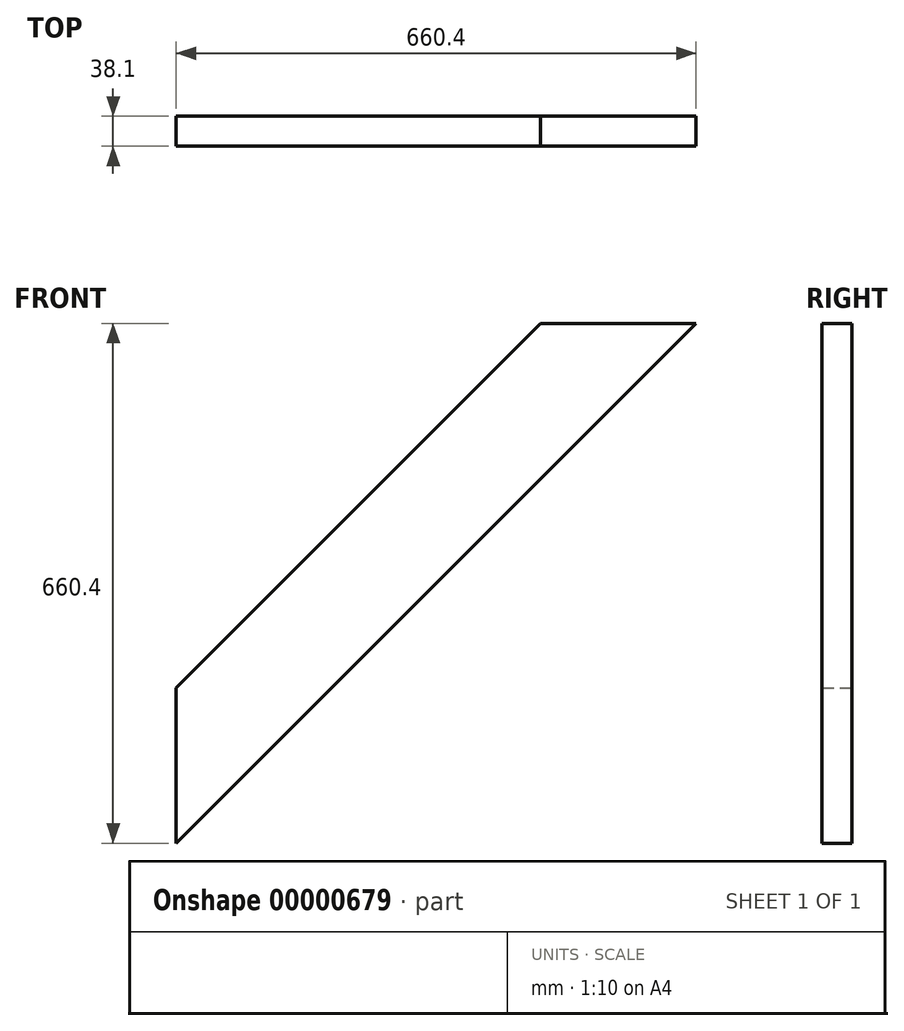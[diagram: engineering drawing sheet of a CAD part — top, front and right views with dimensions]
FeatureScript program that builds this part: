
annotation { "Feature Type Name" : "Feature", "Feature Type Description" : "" }
export const myFeature = defineFeature(function(context is Context, id is Id, definition is map)
    precondition{}
    {
        {
            var Q0;
            Q0=qCreatedBy(makeId("Front.planeOp"),FACE);
            var sketch = newSketch(context, id + "F0", { "sketchPlane" : qUnion([Q0])});
            skLineSegment(sketch, "E0", {"start": v(181.36, 197.57) * mm, "end": v(644.2, 660.4) * mm});
            skLineSegment(sketch, "E1", {"start": v(644.2, 660.4) * mm, "end": v(841.76, 660.4) * mm});
            skLineSegment(sketch, "E2", {"start": v(841.76, 660.4) * mm, "end": v(181.36, 0) * mm});
            skLineSegment(sketch, "E3", {"start": v(181.36, 0) * mm, "end": v(181.36, 197.57) * mm});
            skLineSegment(sketch, "E4", {"start": v(181.36, 0) * mm, "end": v(935.54, 0) * mm, "construction": true});
            skSolve(sketch);
        }
        {
            var Q0;
            Q0=makeQuery(id+"F0.imprint","IMPRINT",FACE,{"disambiguationData":[TD([[makeQuery(id+"F0.imprint","IMPRINT",EDGE,{"derivedFrom":sQuery(id+"F0.wireOp",EDGE,"E0")}),-1.0]])]});
            extrude(context, id + "F1", {"entities" : qUnion([Q0]), "depth" : 38.1 * mm});
        }
    });
